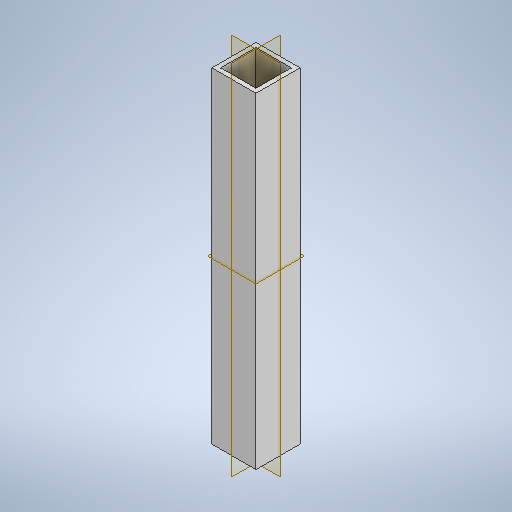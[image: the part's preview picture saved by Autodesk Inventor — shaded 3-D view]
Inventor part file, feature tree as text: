
AUTODESK INVENTOR PART (.ipt)
format: ipt  version: 2025.2 (Build 292293000, 293)  size: 253,440 bytes
history: native  units: mm
features: other x1, extrude x1, sketch x1
ambient origin geometry x8: Origin, YZ Plane, XZ Plane, XY Plane, X Axis, Y Axis, Z Axis, Center Point
bodies: Body1 (feature_tree)
feature tree (3):
  other  "Sólido1"
  extrude  "Extrusão1"  Depth=10.0mm
  sketch  "Esboço1"  dims[d0=100.0mm d1=10.0mm d2=740.0mm d3=0.0mm]
